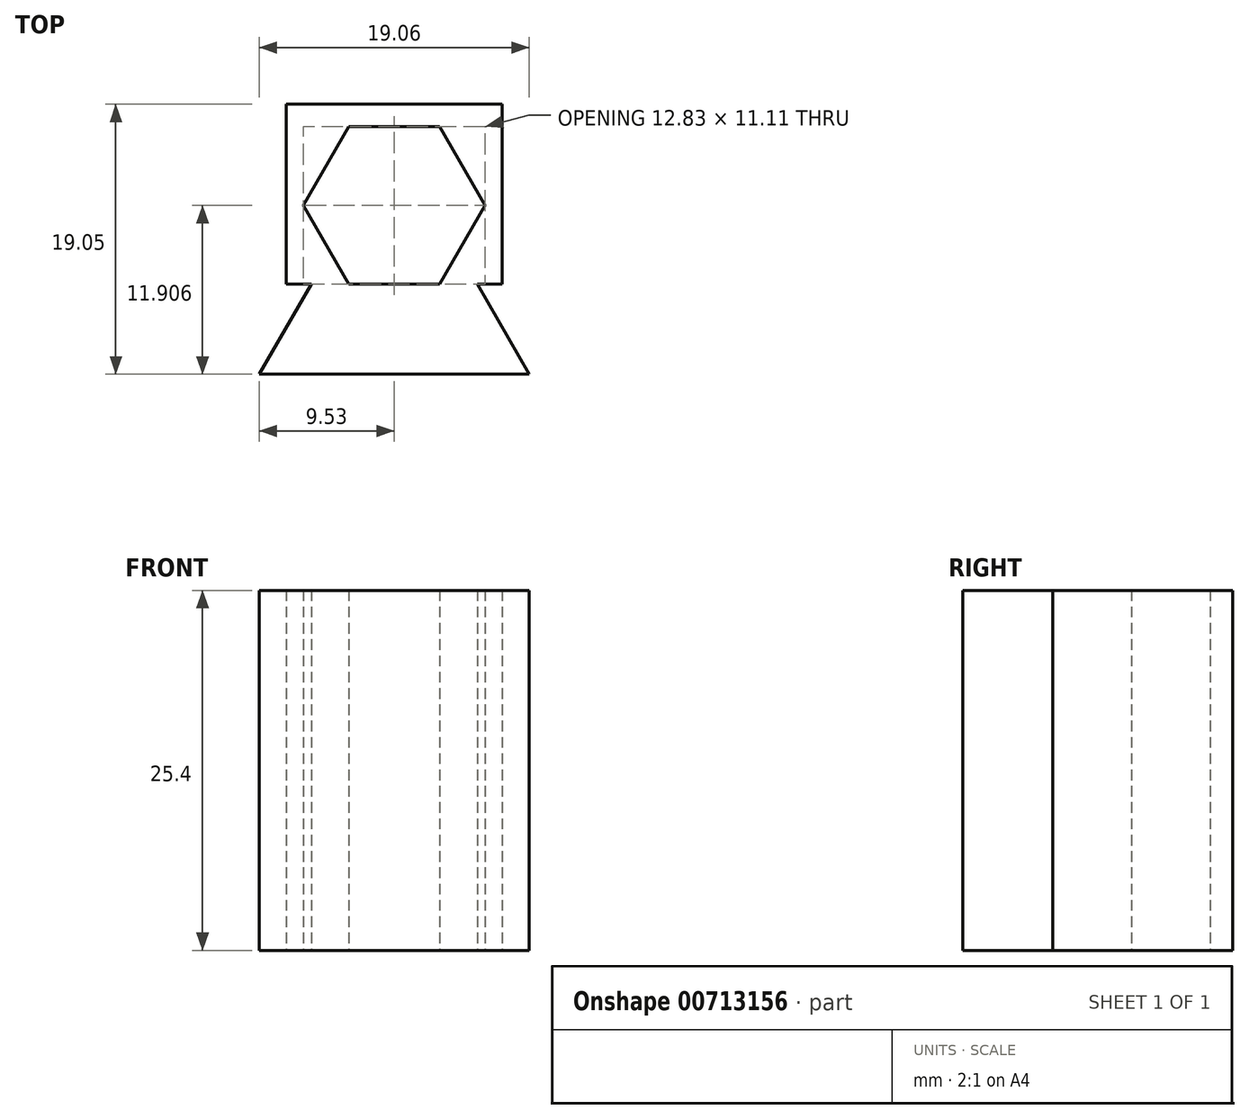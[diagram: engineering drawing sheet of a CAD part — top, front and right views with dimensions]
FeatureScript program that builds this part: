
annotation { "Feature Type Name" : "Feature", "Feature Type Description" : "" }
export const myFeature = defineFeature(function(context is Context, id is Id, definition is map)
    precondition{}
    {
        {
            var Q0;
            Q0=qCreatedBy(makeId("Top.planeOp"),FACE);
            var sketch = newSketch(context, id + "F0", { "sketchPlane" : qUnion([Q0])});
            skLineSegment(sketch, "E0.bottom", {"start": v(-7.62, 0) * mm, "end": v(-5.86, 0) * mm});
            skLineSegment(sketch, "E0.top", {"start": v(-7.62, 12.7) * mm, "end": v(7.62, 12.7) * mm});
            skLineSegment(sketch, "E0.left", {"start": v(-7.62, 0) * mm, "end": v(-7.62, 12.7) * mm});
            skLineSegment(sketch, "E0.right", {"start": v(7.62, 0) * mm, "end": v(7.62, 12.7) * mm});
            skLineSegment(sketch, "E1", {"start": v(-5.86, 0) * mm, "end": v(-9.53, -6.35) * mm});
            skLineSegment(sketch, "E2", {"start": v(-9.53, -6.35) * mm, "end": v(9.53, -6.35) * mm});
            skLineSegment(sketch, "E3", {"start": v(9.53, -6.35) * mm, "end": v(5.86, 0) * mm});
            skCircle(sketch, "E4.cCircle", {"center": v(0, 5.56) * mm, "radius": 5.56 * mm, "construction": true});
            skLineSegment(sketch, "E4.0", {"start": v(3.2, 0) * mm, "end": v(-3.2, 0) * mm});
            skLineSegment(sketch, "E4.1", {"start": v(-3.2, 0) * mm, "end": v(-6.42, 5.56) * mm});
            skLineSegment(sketch, "E4.2", {"start": v(-6.42, 5.56) * mm, "end": v(-3.2, 11.11) * mm});
            skLineSegment(sketch, "E4.3", {"start": v(-3.2, 11.11) * mm, "end": v(3.2, 11.11) * mm});
            skLineSegment(sketch, "E4.4", {"start": v(3.2, 11.11) * mm, "end": v(6.42, 5.56) * mm});
            skLineSegment(sketch, "E4.5", {"start": v(6.42, 5.56) * mm, "end": v(3.2, 0) * mm});
            skPoint(sketch, "E4.0.midPoint", {"position": v(0, 0) * mm});
            skLineSegment(sketch, "E5.trimOffspring", {"start": v(5.86, 0) * mm, "end": v(7.62, 0) * mm});
            skLineSegment(sketch, "E6", {"start": v(0, 5.56) * mm, "end": v(0, 0) * mm, "construction": true});
            skLineSegment(sketch, "E7", {"start": v(0, -6.35) * mm, "end": v(0, 0) * mm, "construction": true});
            skSolve(sketch);
        }
        {
            var Q0;
            Q0=makeQuery(id+"F0.imprint","IMPRINT",FACE,{"disambiguationData":[TD([[makeQuery(id+"F0.imprint","IMPRINT",EDGE,{"derivedFrom":sQuery(id+"F0.wireOp",EDGE,"E0.bottom")}),1.0]])]});
            extrude(context, id + "F1", {"entities" : qUnion([Q0]), "depth" : 25.4 * mm, "offsetDistance" : 25.4 * mm});
        }
    });
